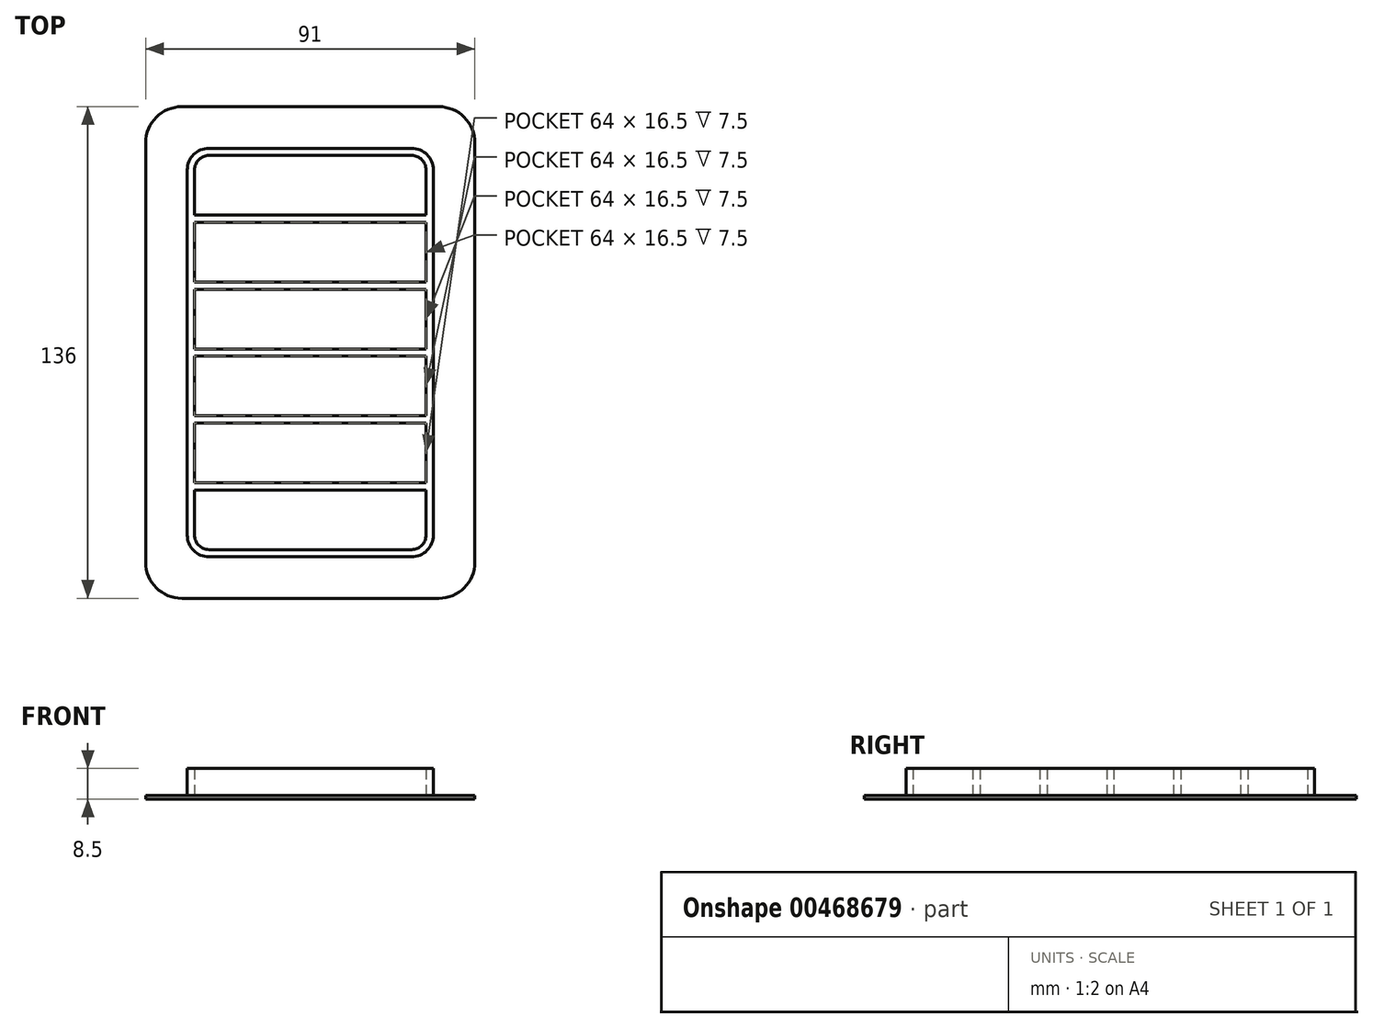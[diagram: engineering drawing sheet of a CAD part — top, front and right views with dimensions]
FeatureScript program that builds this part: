
annotation { "Feature Type Name" : "Feature", "Feature Type Description" : "" }
export const myFeature = defineFeature(function(context is Context, id is Id, definition is map)
    precondition{}
    {
        {
            var Q0;
            Q0=qCreatedBy(makeId("Top.planeOp"),FACE);
            var sketch = newSketch(context, id + "F0", { "sketchPlane" : qUnion([Q0])});
            skLineSegment(sketch, "E0.bottom", {"start": v(-28.5, 44.67) * mm, "end": v(27.5, 44.67) * mm});
            skLineSegment(sketch, "E0.top", {"start": v(-28.5, -76.33) * mm, "end": v(27.5, -76.33) * mm});
            skLineSegment(sketch, "E0.left", {"start": v(-38.5, 34.67) * mm, "end": v(-38.5, -66.33) * mm});
            skLineSegment(sketch, "E0.right", {"start": v(37.5, 34.67) * mm, "end": v(37.5, -66.33) * mm});
            skPoint(sketch, "E1.visualSharp", {"position": v(-38.5, 44.67) * mm});
            skArc(sketch, "E1.filletArc", {"start": v(-28.5, 44.67) * mm, "mid": v(-35.58, 41.74) * mm, "end": v(-38.5, 34.67) * mm});
            skPoint(sketch, "E2.visualSharp", {"position": v(37.5, 44.67) * mm});
            skArc(sketch, "E2.filletArc", {"start": v(37.5, 34.67) * mm, "mid": v(34.57, 41.74) * mm, "end": v(27.5, 44.67) * mm});
            skPoint(sketch, "E3.visualSharp", {"position": v(37.5, -76.33) * mm});
            skArc(sketch, "E3.filletArc", {"start": v(27.5, -76.33) * mm, "mid": v(34.57, -73.4) * mm, "end": v(37.5, -66.33) * mm});
            skPoint(sketch, "E4.visualSharp", {"position": v(-38.5, -76.33) * mm});
            skArc(sketch, "E4.filletArc", {"start": v(-38.5, -66.33) * mm, "mid": v(-35.58, -73.4) * mm, "end": v(-28.5, -76.33) * mm});
            skLineSegment(sketch, "E5.bottom", {"start": v(-36, 52.17) * mm, "end": v(35, 52.17) * mm});
            skLineSegment(sketch, "E5.top", {"start": v(-36, -83.83) * mm, "end": v(35, -83.83) * mm});
            skLineSegment(sketch, "E5.left", {"start": v(-46, 42.17) * mm, "end": v(-46, -73.83) * mm});
            skLineSegment(sketch, "E5.right", {"start": v(45, 42.17) * mm, "end": v(45, -73.83) * mm});
            skPoint(sketch, "E6.visualSharp", {"position": v(-46, 52.17) * mm});
            skArc(sketch, "E6.filletArc", {"start": v(-36, 52.17) * mm, "mid": v(-43.08, 49.24) * mm, "end": v(-46, 42.17) * mm});
            skPoint(sketch, "E7.visualSharp", {"position": v(45, 52.17) * mm});
            skArc(sketch, "E7.filletArc", {"start": v(45, 42.17) * mm, "mid": v(42.07, 49.24) * mm, "end": v(35, 52.17) * mm});
            skPoint(sketch, "E8.visualSharp", {"position": v(45, -83.83) * mm});
            skArc(sketch, "E8.filletArc", {"start": v(35, -83.83) * mm, "mid": v(42.07, -80.9) * mm, "end": v(45, -73.83) * mm});
            skPoint(sketch, "E9.visualSharp", {"position": v(-46, -83.83) * mm});
            skArc(sketch, "E9.filletArc", {"start": v(-46, -73.83) * mm, "mid": v(-43.08, -80.9) * mm, "end": v(-36, -83.83) * mm});
            skLineSegment(sketch, "E10.bottom", {"start": v(-28.5, 42.67) * mm, "end": v(27.5, 42.67) * mm});
            skLineSegment(sketch, "E10.top", {"start": v(-28.5, -74.33) * mm, "end": v(27.5, -74.33) * mm});
            skLineSegment(sketch, "E10.left", {"start": v(-36.5, 34.67) * mm, "end": v(-36.5, -66.33) * mm});
            skLineSegment(sketch, "E10.right", {"start": v(35.5, 34.67) * mm, "end": v(35.5, -66.33) * mm});
            skPoint(sketch, "E11.visualSharp", {"position": v(-36.5, 42.67) * mm});
            skArc(sketch, "E11.filletArc", {"start": v(-28.5, 42.67) * mm, "mid": v(-34.16, 40.32) * mm, "end": v(-36.5, 34.67) * mm});
            skPoint(sketch, "E12.visualSharp", {"position": v(35.5, 42.67) * mm});
            skArc(sketch, "E12.filletArc", {"start": v(35.5, 34.67) * mm, "mid": v(33.15, 40.32) * mm, "end": v(27.5, 42.67) * mm});
            skPoint(sketch, "E13.visualSharp", {"position": v(35.5, -74.33) * mm});
            skArc(sketch, "E13.filletArc", {"start": v(27.5, -74.33) * mm, "mid": v(33.15, -72) * mm, "end": v(35.5, -66.33) * mm});
            skPoint(sketch, "E14.visualSharp", {"position": v(-36.5, -74.33) * mm});
            skArc(sketch, "E14.filletArc", {"start": v(-36.5, -66.33) * mm, "mid": v(-34.16, -72) * mm, "end": v(-28.5, -74.33) * mm});
            skLineSegment(sketch, "E15.bottom", {"start": v(-28.5, 40.67) * mm, "end": v(27.5, 40.67) * mm});
            skLineSegment(sketch, "E15.top", {"start": v(-28.5, -72.33) * mm, "end": v(27.5, -72.33) * mm});
            skLineSegment(sketch, "E15.left", {"start": v(-34.5, 34.67) * mm, "end": v(-34.5, -66.33) * mm});
            skLineSegment(sketch, "E15.right", {"start": v(33.5, 34.67) * mm, "end": v(33.5, -66.33) * mm});
            skPoint(sketch, "E16.visualSharp", {"position": v(-34.5, -72.33) * mm});
            skArc(sketch, "E16.filletArc", {"start": v(-34.5, -66.33) * mm, "mid": v(-32.75, -70.58) * mm, "end": v(-28.5, -72.33) * mm});
            skPoint(sketch, "E17.visualSharp", {"position": v(33.5, -72.33) * mm});
            skArc(sketch, "E17.filletArc", {"start": v(27.5, -72.33) * mm, "mid": v(31.74, -70.58) * mm, "end": v(33.5, -66.33) * mm});
            skPoint(sketch, "E18.visualSharp", {"position": v(33.5, 40.67) * mm});
            skArc(sketch, "E18.filletArc", {"start": v(33.5, 34.67) * mm, "mid": v(31.74, 38.9) * mm, "end": v(27.5, 40.67) * mm});
            skPoint(sketch, "E19.visualSharp", {"position": v(-34.5, 40.67) * mm});
            skArc(sketch, "E19.filletArc", {"start": v(-28.5, 40.67) * mm, "mid": v(-32.75, 38.9) * mm, "end": v(-34.5, 34.67) * mm});
            skLineSegment(sketch, "E20.bottom", {"start": v(-28.5, 38.67) * mm, "end": v(27.5, 38.67) * mm});
            skLineSegment(sketch, "E20.top", {"start": v(-28.5, -70.33) * mm, "end": v(27.5, -70.33) * mm});
            skLineSegment(sketch, "E20.left", {"start": v(-32.5, 34.67) * mm, "end": v(-32.5, -66.33) * mm});
            skLineSegment(sketch, "E20.right", {"start": v(31.5, 34.67) * mm, "end": v(31.5, -66.33) * mm});
            skPoint(sketch, "E21.visualSharp", {"position": v(-32.5, 38.67) * mm});
            skArc(sketch, "E21.filletArc", {"start": v(-28.5, 38.67) * mm, "mid": v(-31.33, 37.5) * mm, "end": v(-32.5, 34.67) * mm});
            skPoint(sketch, "E22.visualSharp", {"position": v(31.5, 38.67) * mm});
            skArc(sketch, "E22.filletArc", {"start": v(31.5, 34.67) * mm, "mid": v(30.32, 37.5) * mm, "end": v(27.5, 38.67) * mm});
            skPoint(sketch, "E23.visualSharp", {"position": v(31.5, -70.33) * mm});
            skArc(sketch, "E23.filletArc", {"start": v(27.5, -70.33) * mm, "mid": v(30.32, -69.16) * mm, "end": v(31.5, -66.33) * mm});
            skPoint(sketch, "E24.visualSharp", {"position": v(-32.5, -70.33) * mm});
            skArc(sketch, "E24.filletArc", {"start": v(-32.5, -66.33) * mm, "mid": v(-31.33, -69.16) * mm, "end": v(-28.5, -70.33) * mm});
            skLineSegment(sketch, "E25.bottom", {"start": v(-32.5, 22.17) * mm, "end": v(31.5, 22.17) * mm});
            skLineSegment(sketch, "E25.top", {"start": v(-32.5, 20.17) * mm, "end": v(31.5, 20.17) * mm});
            skLineSegment(sketch, "E25.left", {"start": v(-32.5, 22.17) * mm, "end": v(-32.5, 20.17) * mm});
            skLineSegment(sketch, "E25.right", {"start": v(31.5, 22.17) * mm, "end": v(31.5, 20.17) * mm});
            skLineSegment(sketch, "E26.bottom", {"start": v(-32.5, 3.67) * mm, "end": v(31.5, 3.67) * mm});
            skLineSegment(sketch, "E26.top", {"start": v(-32.5, 1.67) * mm, "end": v(31.5, 1.67) * mm});
            skLineSegment(sketch, "E26.left", {"start": v(-32.5, 3.67) * mm, "end": v(-32.5, 1.67) * mm});
            skLineSegment(sketch, "E26.right", {"start": v(31.5, 3.67) * mm, "end": v(31.5, 1.67) * mm});
            skLineSegment(sketch, "E27.bottom", {"start": v(-32.5, -14.83) * mm, "end": v(31.5, -14.83) * mm});
            skLineSegment(sketch, "E27.top", {"start": v(-32.5, -16.83) * mm, "end": v(31.5, -16.83) * mm});
            skLineSegment(sketch, "E27.left", {"start": v(-32.5, -14.83) * mm, "end": v(-32.5, -16.83) * mm});
            skLineSegment(sketch, "E27.right", {"start": v(31.5, -14.83) * mm, "end": v(31.5, -16.83) * mm});
            skLineSegment(sketch, "E28.bottom", {"start": v(-32.5, -33.33) * mm, "end": v(31.5, -33.33) * mm});
            skLineSegment(sketch, "E28.top", {"start": v(-32.5, -35.33) * mm, "end": v(31.5, -35.33) * mm});
            skLineSegment(sketch, "E28.left", {"start": v(-32.5, -33.33) * mm, "end": v(-32.5, -35.33) * mm});
            skLineSegment(sketch, "E28.right", {"start": v(31.5, -33.33) * mm, "end": v(31.5, -35.33) * mm});
            skLineSegment(sketch, "E29.bottom", {"start": v(-32.5, -51.83) * mm, "end": v(31.5, -51.83) * mm});
            skLineSegment(sketch, "E29.top", {"start": v(-32.5, -53.83) * mm, "end": v(31.5, -53.83) * mm});
            skLineSegment(sketch, "E29.left", {"start": v(-32.5, -51.83) * mm, "end": v(-32.5, -53.83) * mm});
            skLineSegment(sketch, "E29.right", {"start": v(31.5, -51.83) * mm, "end": v(31.5, -53.83) * mm});
            skSolve(sketch);
        }
        {
            var Q0;
            Q0=makeQuery(id+"F0.imprint","IMPRINT",FACE,{"disambiguationData":[TD([[makeQuery(id+"F0.imprint","IMPRINT",EDGE,{"derivedFrom":sQuery(id+"F0.wireOp",EDGE,"E0.bottom")}),1.0]])]});
            var Q1;
            Q1=makeQuery(id+"F0.imprint","IMPRINT",FACE,{"disambiguationData":[TD([[makeQuery(id+"F0.imprint","IMPRINT",EDGE,{"derivedFrom":sQuery(id+"F0.wireOp",EDGE,"E0.bottom")}),-1.0]])]});
            var Q2;
            Q2=makeQuery(id+"F0.imprint","IMPRINT",FACE,{"disambiguationData":[TD([[makeQuery(id+"F0.imprint","IMPRINT",EDGE,{"derivedFrom":sQuery(id+"F0.wireOp",EDGE,"E10.bottom")}),-1.0]])]});
            var Q3;
            Q3=makeQuery(id+"F0.imprint","IMPRINT",FACE,{"disambiguationData":[TD([[makeQuery(id+"F0.imprint","IMPRINT",EDGE,{"derivedFrom":sQuery(id+"F0.wireOp",EDGE,"E15.bottom")}),-1.0]])]});
            var Q4;
            Q4=makeQuery(id+"F0.imprint","IMPRINT",FACE,{"disambiguationData":[TD([[makeQuery(id+"F0.imprint","IMPRINT",EDGE,{"derivedFrom":sQuery(id+"F0.wireOp",EDGE,"E20.bottom")}),-1.0]])]});
            var Q5;
            {var subQ0=sQuery(id+"F0.wireOp",EDGE,"E25.top");Q5=makeQuery(id+"F0.imprint","IMPRINT",FACE,{"disambiguationData":[TD([[makeQuery(id+"F0.imprint","IMPRINT",EDGE,{"derivedFrom":subQ0}),-1.0]])]});}
            var Q6;
            {var subQ0=sQuery(id+"F0.wireOp",EDGE,"E26.top");Q6=makeQuery(id+"F0.imprint","IMPRINT",FACE,{"disambiguationData":[TD([[makeQuery(id+"F0.imprint","IMPRINT",EDGE,{"derivedFrom":subQ0}),-1.0]])]});}
            var Q7;
            {var subQ0=sQuery(id+"F0.wireOp",EDGE,"E27.top");Q7=makeQuery(id+"F0.imprint","IMPRINT",FACE,{"disambiguationData":[TD([[makeQuery(id+"F0.imprint","IMPRINT",EDGE,{"derivedFrom":subQ0}),-1.0]])]});}
            var Q8;
            {var subQ0=sQuery(id+"F0.wireOp",EDGE,"E28.top");Q8=makeQuery(id+"F0.imprint","IMPRINT",FACE,{"disambiguationData":[TD([[makeQuery(id+"F0.imprint","IMPRINT",EDGE,{"derivedFrom":subQ0}),-1.0]])]});}
            var Q9;
            Q9=makeQuery(id+"F0.imprint","IMPRINT",FACE,{"disambiguationData":[TD([[makeQuery(id+"F0.imprint","IMPRINT",EDGE,{"derivedFrom":sQuery(id+"F0.wireOp",EDGE,"E20.top")}),1.0]])]});
            extrude(context, id + "F1", {"entities" : qUnion([Q0, Q1, Q2, Q3, Q4, Q5, Q6, Q7, Q8, Q9]), "depth" : 1 * mm});
        }
        {
            var Q0;
            Q0=makeQuery(id+"F0.imprint","IMPRINT",FACE,{"disambiguationData":[TD([[makeQuery(id+"F0.imprint","IMPRINT",EDGE,{"derivedFrom":sQuery(id+"F0.wireOp",EDGE,"E15.bottom")}),-1.0]])]});
            extrude(context, id + "F2", {"entities" : qUnion([Q0]), "depth" : 8.5 * mm});
        }
        {
            var Q0;
            Q0=makeQuery(id+"F0.imprint","IMPRINT",FACE,{"disambiguationData":[TD([[makeQuery(id+"F0.imprint","IMPRINT",EDGE,{"derivedFrom":sQuery(id+"F0.wireOp",EDGE,"E25.bottom")}),-1.0]])]});
            var Q1;
            Q1=makeQuery(id+"F0.imprint","IMPRINT",FACE,{"disambiguationData":[TD([[makeQuery(id+"F0.imprint","IMPRINT",EDGE,{"derivedFrom":sQuery(id+"F0.wireOp",EDGE,"E26.bottom")}),-1.0]])]});
            var Q2;
            Q2=makeQuery(id+"F0.imprint","IMPRINT",FACE,{"disambiguationData":[TD([[makeQuery(id+"F0.imprint","IMPRINT",EDGE,{"derivedFrom":sQuery(id+"F0.wireOp",EDGE,"E27.bottom")}),-1.0]])]});
            var Q3;
            Q3=makeQuery(id+"F0.imprint","IMPRINT",FACE,{"disambiguationData":[TD([[makeQuery(id+"F0.imprint","IMPRINT",EDGE,{"derivedFrom":sQuery(id+"F0.wireOp",EDGE,"E28.bottom")}),-1.0]])]});
            var Q4;
            Q4=makeQuery(id+"F0.imprint","IMPRINT",FACE,{"disambiguationData":[TD([[makeQuery(id+"F0.imprint","IMPRINT",EDGE,{"derivedFrom":sQuery(id+"F0.wireOp",EDGE,"E29.bottom")}),-1.0]])]});
            extrude(context, id + "F3", {"entities" : qUnion([Q0, Q1, Q2, Q3, Q4]), "operationType" : NewBodyOperationType.ADD, "depth" : 8.5 * mm});
        }
    });
